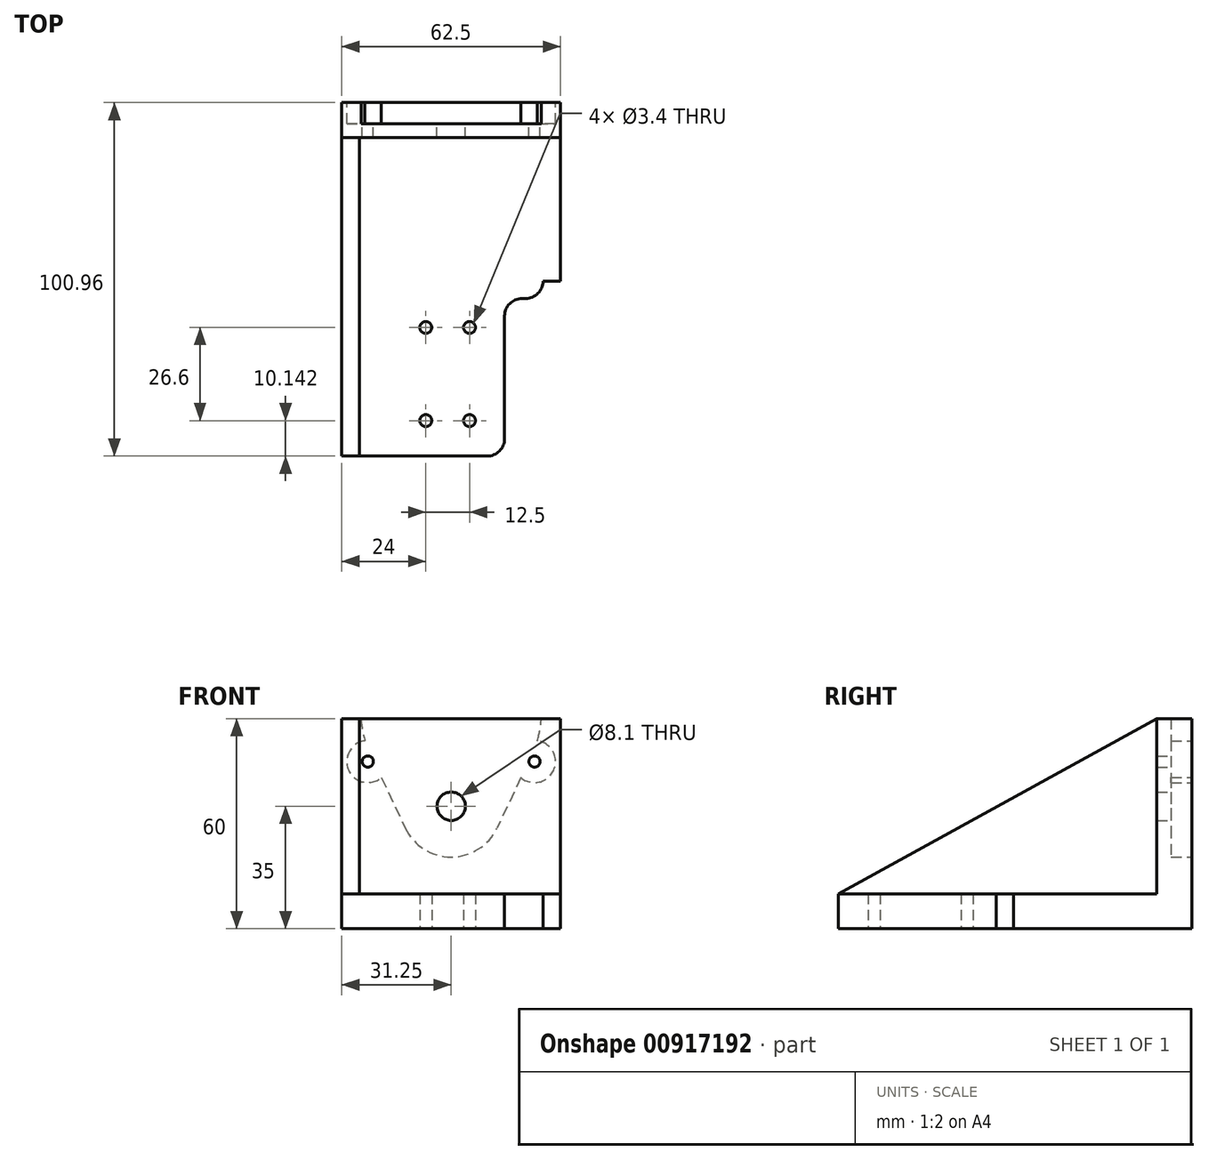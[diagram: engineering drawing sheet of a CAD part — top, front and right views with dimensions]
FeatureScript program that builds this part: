
annotation { "Feature Type Name" : "Feature", "Feature Type Description" : "" }
export const myFeature = defineFeature(function(context is Context, id is Id, definition is map)
    precondition{}
    {
        {
            var Q0;
            Q0=qCreatedBy(makeId("Top.planeOp"),FACE);
            var sketch = newSketch(context, id + "F0", { "sketchPlane" : qUnion([Q0])});
            skLineSegment(sketch, "E0.bottom", {"start": v(-26.25, 50.48) * mm, "end": v(26.25, 50.48) * mm});
            skLineSegment(sketch, "E0.top", {"start": v(-26.25, -50.48) * mm, "end": v(10.25, -50.48) * mm});
            skLineSegment(sketch, "E0.left", {"start": v(-26.25, 50.48) * mm, "end": v(-26.25, -50.48) * mm});
            skLineSegment(sketch, "E0.right", {"start": v(26.25, 50.48) * mm, "end": v(26.25, -0.48) * mm});
            skPoint(sketch, "E0.middle", {"position": v(0, 0) * mm});
            skLineSegment(sketch, "E1.top", {"start": v(21.25, -5.48) * mm, "end": v(20.25, -5.48) * mm});
            skLineSegment(sketch, "E1.right", {"start": v(15.25, -45.48) * mm, "end": v(15.25, -10.48) * mm});
            skPoint(sketch, "E2.visualSharp", {"position": v(15.25, -5.48) * mm});
            skArc(sketch, "E2.filletArc", {"start": v(20.25, -5.48) * mm, "mid": v(16.71, -6.94) * mm, "end": v(15.25, -10.48) * mm});
            skPoint(sketch, "E3.visualSharp", {"position": v(15.25, -50.48) * mm});
            skArc(sketch, "E3.filletArc", {"start": v(10.25, -50.48) * mm, "mid": v(13.79, -49.01) * mm, "end": v(15.25, -45.48) * mm});
            skPoint(sketch, "E4.visualSharp", {"position": v(26.25, -5.47) * mm});
            skArc(sketch, "E4.filletArc", {"start": v(21.25, -5.48) * mm, "mid": v(24.79, -4.01) * mm, "end": v(26.25, -0.48) * mm});
            skCircle(sketch, "E5", {"center": v(-7.25, -13.74) * mm, "radius": 1.7 * mm});
            skCircle(sketch, "E6", {"center": v(-7.25, -40.34) * mm, "radius": 1.7 * mm});
            skCircle(sketch, "E7", {"center": v(5.25, -13.74) * mm, "radius": 1.7 * mm});
            skCircle(sketch, "E8", {"center": v(5.25, -40.34) * mm, "radius": 1.7 * mm});
            skSolve(sketch);
        }
        {
            var Q0;
            Q0 = qSketchRegion(id + "F0", true);
            extrude(context, id + "F1", {"entities" : qUnion([Q0]), "depth" : 10 * mm, "offsetDistance" : 25 * mm});
        }
        {
            var Q0;
            Q0=makeQuery(id+"F1.opExtrude","CAP_FACE",FACE,{"disambiguationData":[OSD([sQuery(id+"F0.wireOp",EDGE,"E0.bottom"),sQuery(id+"F0.wireOp",EDGE,"E0.top"),sQuery(id+"F0.wireOp",EDGE,"E0.left"),sQuery(id+"F0.wireOp",EDGE,"E0.right"),sQuery(id+"F0.wireOp",EDGE,"E1.top"),sQuery(id+"F0.wireOp",EDGE,"E1.right"),sQuery(id+"F0.wireOp",EDGE,"E2.filletArc"),sQuery(id+"F0.wireOp",EDGE,"E3.filletArc"),sQuery(id+"F0.wireOp",EDGE,"E4.filletArc"),sQuery(id+"F0.wireOp",EDGE,"E5"),sQuery(id+"F0.wireOp",EDGE,"E6"),sQuery(id+"F0.wireOp",EDGE,"E7"),sQuery(id+"F0.wireOp",EDGE,"E8")])],"isStart":false});
            var sketch = newSketch(context, id + "F2", { "sketchPlane" : qUnion([Q0])});
            skLineSegment(sketch, "E9.bottom", {"start": v(-26.25, 50.48) * mm, "end": v(26.25, 50.48) * mm});
            skLineSegment(sketch, "E9.top", {"start": v(-26.25, 40.48) * mm, "end": v(26.25, 40.48) * mm});
            skLineSegment(sketch, "E9.left", {"start": v(-26.25, 50.48) * mm, "end": v(-26.25, 40.48) * mm});
            skLineSegment(sketch, "E9.right", {"start": v(26.25, 50.48) * mm, "end": v(26.25, 40.48) * mm});
            skLineSegment(sketch, "E10.bottom", {"start": v(-26.25, -50.48) * mm, "end": v(-21.25, -50.48) * mm});
            skLineSegment(sketch, "E10.top", {"start": v(-26.25, 40.48) * mm, "end": v(-21.25, 40.48) * mm});
            skLineSegment(sketch, "E10.left", {"start": v(-26.25, -50.47) * mm, "end": v(-26.25, 40.48) * mm});
            skLineSegment(sketch, "E10.right", {"start": v(-21.25, -50.47) * mm, "end": v(-21.25, 40.48) * mm});
            skSolve(sketch);
        }
        {
            var Q0;
            Q0=makeQuery(id+"F2.imprint","IMPRINT",FACE,{"disambiguationData":[TD([[makeQuery(id+"F2.imprint","IMPRINT",EDGE,{"derivedFrom":sQuery(id+"F2.wireOp",EDGE,"E9.bottom")}),-1.0]])]});
            extrude(context, id + "F3", {"entities" : qUnion([Q0]), "operationType" : NewBodyOperationType.ADD, "depth" : 50 * mm, "offsetDistance" : 25 * mm});
        }
        {
            var Q0;
            Q0=makeQuery(id+"F3.boolean.opBoolean","MERGE",FACE,{"derivedFrom":[makeQuery(id+"F1.opExtrude","SWEPT_FACE",FACE,{"disambiguationData":[OSD([sQuery(id+"F0.wireOp",EDGE,"E0.bottom")])]}),makeQuery(id+"F3.opExtrude","SWEPT_FACE",FACE,{"disambiguationData":[OSD([sQuery(id+"F2.wireOp",EDGE,"E9.bottom")])]})]});
            var sketch = newSketch(context, id + "F4", { "sketchPlane" : qUnion([Q0])});
            skCircle(sketch, "E11", {"center": v(0, 35) * mm, "radius": 4.05 * mm});
            skArc(sketch, "E12", {"start": v(23.27, 50.21) * mm, "mid": v(0, 87) * mm, "end": v(-23.27, 50.21) * mm});
            skArc(sketch, "E13", {"start": v(-13.1, 28.79) * mm, "mid": v(0, 20.5) * mm, "end": v(13.1, 28.79) * mm});
            skLineSegment(sketch, "E14", {"start": v(-23.27, 50.21) * mm, "end": v(-13.1, 28.79) * mm});
            skLineSegment(sketch, "E15", {"start": v(23.27, 50.21) * mm, "end": v(13.1, 28.79) * mm});
            skSolve(sketch);
        }
        {
            var Q0;
            Q0=makeQuery(id+"F4.imprint","IMPRINT",FACE,{"disambiguationData":[TD([[makeQuery(id+"F4.imprint","IMPRINT",EDGE,{"derivedFrom":sQuery(id+"F4.wireOp",EDGE,"E11")}),-1.0]])]});
            var Q1;
            Q1=makeQuery(id+"F4.imprint","IMPRINT",FACE,{"disambiguationData":[TD([[makeQuery(id+"F4.imprint","IMPRINT",EDGE,{"derivedFrom":sQuery(id+"F4.wireOp",EDGE,"E11")}),1.0]])]});
            extrude(context, id + "F5", {"entities" : qUnion([Q0, Q1]), "operationType" : NewBodyOperationType.REMOVE, "oppositeDirection" : true, "depth" : 6 * mm, "offsetDistance" : 25 * mm});
        }
        {
            var Q0;
            Q0=makeQuery(id+"F3.boolean.opBoolean","MERGE",FACE,{"derivedFrom":[makeQuery(id+"F1.opExtrude","SWEPT_FACE",FACE,{"disambiguationData":[OSD([sQuery(id+"F0.wireOp",EDGE,"E0.bottom")])]}),makeQuery(id+"F3.opExtrude","SWEPT_FACE",FACE,{"disambiguationData":[OSD([sQuery(id+"F2.wireOp",EDGE,"E9.bottom")])]})]});
            var sketch = newSketch(context, id + "F6", { "sketchPlane" : qUnion([Q0])});
            skCircle(sketch, "E16", {"center": v(0, 35) * mm, "radius": 4.05 * mm});
            skCircle(sketch, "E17", {"center": v(-23.8, 47.75) * mm, "radius": 1.6 * mm});
            skCircle(sketch, "E18", {"center": v(23.8, 47.75) * mm, "radius": 1.6 * mm});
            skSolve(sketch);
        }
        {
            var Q0;
            Q0=makeQuery(id+"F6.imprint","IMPRINT",FACE,{"disambiguationData":[TD([[makeQuery(id+"F6.imprint","IMPRINT",EDGE,{"derivedFrom":sQuery(id+"F6.wireOp",EDGE,"E16")}),1.0]])]});
            var Q1;
            Q1=makeQuery(id+"F6.imprint","IMPRINT",FACE,{"disambiguationData":[TD([[makeQuery(id+"F6.imprint","IMPRINT",EDGE,{"derivedFrom":sQuery(id+"F6.wireOp",EDGE,"E17")}),1.0]])]});
            var Q2;
            Q2=makeQuery(id+"F6.imprint","IMPRINT",FACE,{"disambiguationData":[TD([[makeQuery(id+"F6.imprint","IMPRINT",EDGE,{"derivedFrom":sQuery(id+"F6.wireOp",EDGE,"E18")}),1.0]])]});
            var Q3;
            Q3=sQuery(id+"F6.wireOp",EDGE,"E17");
            var Q4;
            Q4=sQuery(id+"F6.wireOp",EDGE,"E16");
            var Q5;
            Q5=sQuery(id+"F6.wireOp",EDGE,"E18");
            extrude(context, id + "F7", {"entities" : qUnion([Q0, Q1, Q2]), "operationType" : NewBodyOperationType.REMOVE, "surfaceEntities" : qUnion([Q3, Q4, Q5]), "oppositeDirection" : true, "depth" : 25 * mm, "offsetDistance" : 25 * mm});
        }
        {
            var Q0;
            Q0=makeQuery(id+"F3.boolean.opBoolean","MERGE",FACE,{"derivedFrom":[makeQuery(id+"F1.opExtrude","SWEPT_FACE",FACE,{"disambiguationData":[OSD([sQuery(id+"F0.wireOp",EDGE,"E0.left")])]}),makeQuery(id+"F3.opExtrude","SWEPT_FACE",FACE,{"disambiguationData":[OSD([sQuery(id+"F2.wireOp",EDGE,"E9.left")])]})]});
            extrude(context, id + "F8", {"entities" : qUnion([Q0]), "operationType" : NewBodyOperationType.ADD, "depth" : 5 * mm, "offsetDistance" : 25 * mm});
        }
        {
            var Q0;
            Q0=makeQuery(id+"F3.boolean.opBoolean","MERGE",FACE,{"derivedFrom":[makeQuery(id+"F1.opExtrude","SWEPT_FACE",FACE,{"disambiguationData":[OSD([sQuery(id+"F0.wireOp",EDGE,"E0.right")])]}),makeQuery(id+"F3.opExtrude","SWEPT_FACE",FACE,{"disambiguationData":[OSD([sQuery(id+"F2.wireOp",EDGE,"E9.right")])]})]});
            extrude(context, id + "F9", {"entities" : qUnion([Q0]), "operationType" : NewBodyOperationType.ADD, "depth" : 5 * mm, "offsetDistance" : 25 * mm});
        }
        {
            var Q0;
            Q0=makeQuery(id+"F8.opExtrude","CAP_FACE",FACE,{"disambiguationData":[OSD([sQuery(id+"F0.wireOp",EDGE,"E0.left"),sQuery(id+"F2.wireOp",EDGE,"E9.left")])],"isStart":false});
            var sketch = newSketch(context, id + "F10", { "sketchPlane" : qUnion([Q0])});
            skLineSegment(sketch, "E19", {"start": v(-40.47, 60) * mm, "end": v(50.48, 10) * mm});
            skSolve(sketch);
        }
        {
            var Q0;
            Q0=makeQuery(id+"F10.imprint","IMPRINT",FACE,{"disambiguationData":[TD([[makeQuery(id+"F10.imprint","IMPRINT",EDGE,{"derivedFrom":sQuery(id+"F10.wireOp",EDGE,"E19")}),-1.0]])]});
            extrude(context, id + "F11", {"entities" : qUnion([Q0]), "operationType" : NewBodyOperationType.ADD, "oppositeDirection" : true, "depth" : 5 * mm, "offsetDistance" : 25 * mm});
        }
        {
            var Q0;
            {var subQ0=sQuery(id+"F2.wireOp",EDGE,"E9.bottom");var subQ1=sQuery(id+"F0.wireOp",EDGE,"E0.bottom");Q0=makeQuery(id+"F9.boolean.opBoolean","MERGE",FACE,{"derivedFrom":[makeQuery(id+"F8.boolean.opBoolean","MERGE",FACE,{"derivedFrom":[makeQuery(id+"F3.boolean.opBoolean","MERGE",FACE,{"derivedFrom":[makeQuery(id+"F1.opExtrude","SWEPT_FACE",FACE,{"disambiguationData":[OSD([subQ1])]}),makeQuery(id+"F3.opExtrude","SWEPT_FACE",FACE,{"disambiguationData":[OSD([subQ0])]})]}),makeQuery(id+"F8.opExtrude","SWEPT_FACE",FACE,{"disambiguationData":[OSD([subQ1,sQuery(id+"F0.wireOp",EDGE,"E0.left"),subQ0,sQuery(id+"F2.wireOp",EDGE,"E9.left")])]})]}),makeQuery(id+"F9.opExtrude","SWEPT_FACE",FACE,{"disambiguationData":[OSD([subQ1,sQuery(id+"F0.wireOp",EDGE,"E0.right"),subQ0,sQuery(id+"F2.wireOp",EDGE,"E9.right")])]})]});}
            var sketch = newSketch(context, id + "F12", { "sketchPlane" : qUnion([Q0])});
            skPoint(sketch, "E20", {"position": v(-23.8, 47.75) * mm});
            skPoint(sketch, "E21", {"position": v(23.8, 47.75) * mm});
            skSolve(sketch);
        }
        {
            var Q0;
            Q0=sQuery(id+"F12.wireOp",VERTEX,"E20");
            var Q1;
            Q1=sQuery(id+"F12.wireOp",VERTEX,"E21");
            var Q2;
            Q2=makeQuery(id+"F1.opExtrude","SWEPT_BODY",BODY,{"disambiguationData":[OSD([sQuery(id+"F0.wireOp",EDGE,"E0.bottom"),sQuery(id+"F0.wireOp",EDGE,"E0.top"),sQuery(id+"F0.wireOp",EDGE,"E0.left"),sQuery(id+"F0.wireOp",EDGE,"E0.right"),sQuery(id+"F0.wireOp",EDGE,"E1.top"),sQuery(id+"F0.wireOp",EDGE,"E1.right"),sQuery(id+"F0.wireOp",EDGE,"E2.filletArc"),sQuery(id+"F0.wireOp",EDGE,"E3.filletArc"),sQuery(id+"F0.wireOp",EDGE,"E4.filletArc"),sQuery(id+"F0.wireOp",EDGE,"E5"),sQuery(id+"F0.wireOp",EDGE,"E6"),sQuery(id+"F0.wireOp",EDGE,"E7"),sQuery(id+"F0.wireOp",EDGE,"E8")])]});
            hole(context, id + "F13", {"style" : HoleStyle.C_BORE, "endStyle" : HoleEndStyle.THROUGH, "holeDiameter" : 3.2 * mm, "cBoreDiameter" : 12 * mm, "cBoreDepth" : 6 * mm, "majorDiameter" : 5 * mm, "isTappedThrough" : true, "tappedDepth" : 12 * mm, "tapClearance" : 3, "startFromSketch" : true, "locations" : qUnion([Q0, Q1]), "scope" : qUnion([Q2])});
        }
    });
